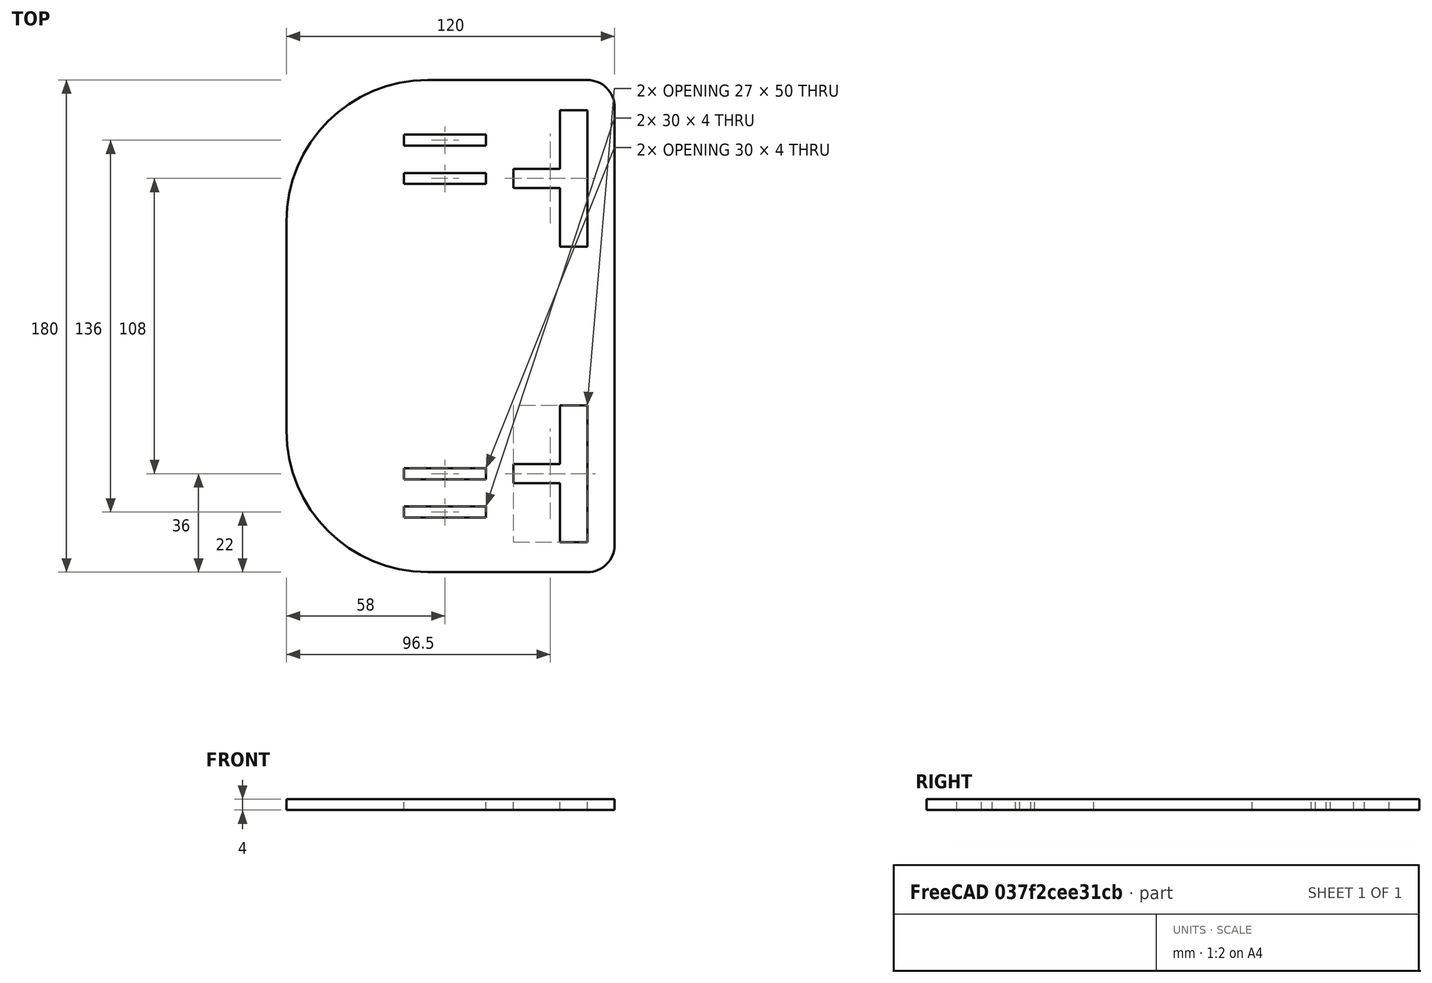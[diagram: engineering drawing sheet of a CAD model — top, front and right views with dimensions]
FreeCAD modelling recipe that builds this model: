
FCSTD DOCUMENT  (FreeCAD 0.21R33771 (Git))
Label: FRAME_BASE
License: All rights reserved
LicenseURL: https://en.wikipedia.org/wiki/All_rights_reserved
objects: Sketcher::SketchObject×2, PartDesign::Pad×1, PartDesign::Body×1
note: 5 computed .brp shape members not serialized (recipe doc carries the construction recipe); baked Part::Feature solids carry a one-line shape summary decoded from their .brp

FEATURE [Sketcher::SketchObject] Sketch  label="A4"
  FullyConstrained = true
  MapMode = 5
  sketch-geometry (4):
    g0: LineSegment StartX=0 StartY=0 StartZ=0 EndX=270 EndY=0 EndZ=0
    g1: LineSegment StartX=270 StartY=0 StartZ=0 EndX=270 EndY=180 EndZ=0
    g2: LineSegment StartX=270 StartY=180 StartZ=0 EndX=0 EndY=180 EndZ=0
    g3: LineSegment StartX=0 StartY=180 StartZ=0 EndX=0 EndY=0 EndZ=0
  constraints (12):
    c: Coincident(g0,g1)
    c: Coincident(g1,g2)
    c: Coincident(g2,g3)
    c: Coincident(g3,g0)
    c: Horizontal(g0)
    c: Horizontal(g2)
    c: Vertical(g1)
    c: Vertical(g3)
    c: PointOnObject(g0,g-2)
    c: DistanceX(g2,g2) = 270
    c: DistanceY(g3,g3) = 180
    c: PointOnObject(g0,g-1)
FEATURE [Sketcher::SketchObject] Sketch001  label="BASE"
  ExternalGeometry = -> [Sketch]
  FullyConstrained = false
  MapMode = 5
  sketch-geometry (57):
    g0: LineSegment StartX=100 StartY=61 StartZ=0 EndX=100 EndY=39.5 EndZ=0
    g1: LineSegment StartX=100 StartY=39.5 StartZ=0 EndX=83 EndY=39.5 EndZ=0
    g2: LineSegment StartX=83 StartY=39.5 StartZ=0 EndX=83 EndY=32.5 EndZ=0
    g3: LineSegment StartX=83 StartY=32.5 StartZ=0 EndX=100 EndY=32.5 EndZ=0
    g4: LineSegment StartX=100 StartY=32.5 StartZ=0 EndX=100 EndY=11 EndZ=0
    g5: LineSegment StartX=100 StartY=11 StartZ=0 EndX=110 EndY=11 EndZ=0
    g6: LineSegment StartX=110 StartY=11 StartZ=0 EndX=110 EndY=61 EndZ=0
    g7: LineSegment StartX=110 StartY=61 StartZ=0 EndX=100 EndY=61 EndZ=0
    g8: LineSegment StartX=100 StartY=119 StartZ=0 EndX=110 EndY=119 EndZ=0
    g9: LineSegment StartX=110 StartY=119 StartZ=0 EndX=110 EndY=169 EndZ=0
    g10: LineSegment StartX=110 StartY=169 StartZ=0 EndX=100 EndY=169 EndZ=0
    g11: LineSegment StartX=100 StartY=169 StartZ=0 EndX=100 EndY=147.5 EndZ=0
    g12: LineSegment StartX=100 StartY=147.5 StartZ=0 EndX=83 EndY=147.5 EndZ=0
    g13: LineSegment StartX=83 StartY=147.5 StartZ=0 EndX=83 EndY=140.5 EndZ=0
    g14: LineSegment StartX=83 StartY=140.5 StartZ=0 EndX=100 EndY=140.5 EndZ=0
    g15: LineSegment StartX=100 StartY=140.5 StartZ=0 EndX=100 EndY=119 EndZ=0
    g16: LineSegment StartX=0 StartY=90 StartZ=0 EndX=0 EndY=128.27 EndZ=0
    g17: LineSegment StartX=51.7304 StartY=180 StartZ=0 EndX=110 EndY=180 EndZ=0
    g18: LineSegment StartX=120 StartY=170 StartZ=0 EndX=120 EndY=10 EndZ=0
    g19: LineSegment StartX=110 StartY=0 StartZ=0 EndX=51.7304 EndY=0 EndZ=0
    g20: LineSegment StartX=0 StartY=51.7304 StartZ=0 EndX=0 EndY=90 EndZ=0
    g21: ArcOfCircle CenterX=51.7304 CenterY=128.27 CenterZ=0 NormalX=0 NormalY=0 NormalZ=1 AngleXU=0 Radius=51.7304 StartAngle=1.5708 EndAngle=3.14159
    g22: GeomPoint X=0 Y=180 Z=0
    g23: ArcOfCircle CenterX=51.7304 CenterY=51.7304 CenterZ=0 NormalX=0 NormalY=0 NormalZ=1 AngleXU=0 Radius=51.7304 StartAngle=3.14159 EndAngle=4.71239
    g24: GeomPoint X=0 Y=0 Z=0
    g25: ArcOfCircle CenterX=110 CenterY=170 CenterZ=0 NormalX=0 NormalY=0 NormalZ=1 AngleXU=0 Radius=10 StartAngle=-9e-16 EndAngle=1.5708
    g26: GeomPoint X=120 Y=180 Z=0
    g27: ArcOfCircle CenterX=110 CenterY=10 CenterZ=0 NormalX=0 NormalY=0 NormalZ=1 AngleXU=0 Radius=10 StartAngle=4.71239 EndAngle=6.28319
    g28: GeomPoint X=120 Y=0 Z=0
    g29: LineSegment StartX=73 StartY=38 StartZ=0 EndX=43 EndY=38 EndZ=0
    g30: LineSegment StartX=43 StartY=38 StartZ=0 EndX=43 EndY=34 EndZ=0
    g31: LineSegment StartX=43 StartY=34 StartZ=0 EndX=73 EndY=34 EndZ=0
    g32: LineSegment StartX=73 StartY=34 StartZ=0 EndX=73 EndY=36 EndZ=0
    g33: LineSegment StartX=73 StartY=36 StartZ=0 EndX=73 EndY=38 EndZ=0
    g34: LineSegment StartX=83 StartY=32.5 StartZ=0 EndX=73 EndY=36 EndZ=0
    g35: LineSegment StartX=73 StartY=36 StartZ=0 EndX=83 EndY=39.5 EndZ=0
    g36: LineSegment StartX=83 StartY=147.5 StartZ=0 EndX=73 EndY=144 EndZ=0
    g37: LineSegment StartX=83 StartY=140.5 StartZ=0 EndX=73 EndY=144 EndZ=0
    g38: LineSegment StartX=73 StartY=144 StartZ=0 EndX=73 EndY=146 EndZ=0
    g39: LineSegment StartX=73 StartY=142 StartZ=0 EndX=73 EndY=144 EndZ=0
    g40: LineSegment StartX=73 StartY=38 StartZ=0 EndX=73 EndY=144 EndZ=0
    g41: LineSegment StartX=73 StartY=146 StartZ=0 EndX=43 EndY=146 EndZ=0
    g42: LineSegment StartX=43 StartY=146 StartZ=0 EndX=43 EndY=142 EndZ=0
    g43: LineSegment StartX=43 StartY=142 StartZ=0 EndX=73 EndY=142 EndZ=0
    g44: LineSegment StartX=43 StartY=38 StartZ=0 EndX=43 EndY=142 EndZ=0
    g45: LineSegment StartX=43 StartY=160 StartZ=0 EndX=43 EndY=156 EndZ=0
    g46: LineSegment StartX=43 StartY=156 StartZ=0 EndX=73 EndY=156 EndZ=0
    g47: LineSegment StartX=73 StartY=156 StartZ=0 EndX=73 EndY=160 EndZ=0
    g48: LineSegment StartX=73 StartY=160 StartZ=0 EndX=43 EndY=160 EndZ=0
    g49: LineSegment StartX=43 StartY=24 StartZ=0 EndX=43 EndY=20 EndZ=0
    g50: LineSegment StartX=43 StartY=20 StartZ=0 EndX=73 EndY=20 EndZ=0
    g51: LineSegment StartX=73 StartY=20 StartZ=0 EndX=73 EndY=24 EndZ=0
    g52: LineSegment StartX=73 StartY=24 StartZ=0 EndX=43 EndY=24 EndZ=0
    g53: LineSegment StartX=43 StartY=24 StartZ=0 EndX=43 EndY=34 EndZ=0
    g54: LineSegment StartX=100 StartY=61 StartZ=0 EndX=100 EndY=90 EndZ=0
    g55: LineSegment StartX=100 StartY=90 StartZ=0 EndX=100 EndY=119 EndZ=0
    g56: LineSegment StartX=0 StartY=90 StartZ=0 EndX=100 EndY=90 EndZ=0
  constraints (154):
    c: Vertical(g0)
    c: Coincident(g1,g0)
    c: Coincident(g2,g1)
    c: Vertical(g2)
    c: Coincident(g3,g2)
    c: Horizontal(g3)
    c: Coincident(g4,g3)
    c: Vertical(g4)
    c: Coincident(g5,g4)
    c: Coincident(g6,g5)
    c: Vertical(g6)
    c: Coincident(g7,g6)
    c: Coincident(g7,g0)
    c: Horizontal(g7)
    c: Horizontal(g1)
    c: Horizontal(g5)
    c: Equal(g0,g4)
    c: Equal(g1,g3)
    c: DistanceY(g2,g2) = 7
    c: DistanceX(g1,g1) = 17
    c: DistanceX(g7,g7) = 10
    c: DistanceY(g6,g6) = 50
    c: Horizontal(g8)
    c: Coincident(g9,g8)
    c: Vertical(g9)
    c: PointOnObject(g10,g9)
    c: Horizontal(g10)
    c: Coincident(g11,g10)
    c: Vertical(g11)
    c: Coincident(g12,g11)
    c: Horizontal(g12)
    c: Coincident(g13,g12)
    c: Vertical(g13)
    c: Coincident(g14,g13)
    c: Horizontal(g14)
    c: Coincident(g15,g14)
    c: Vertical(g15)
    c: Equal(g15,g11)
    c: Equal(g14,g1)
    c: Equal(g8,g7)
    c: Equal(g13,g2)
    c: Vertical(g11,g14)
    c: PointOnObject(g9,g10)
    c: Equal(g6,g9)
    c: DistanceY(g0,g8) = 58
    c: Vertical(g16)
    c: Horizontal(g17)
    c: Vertical(g18)
    c: Horizontal(g19)
    c: Vertical(g20)
    c: DistanceX(g9,g26) = 10
    c: DistanceX(g24,g28) = 120
    c: DistanceY(g24,g22) = 180
    c: PointOnObject(g22,g16)
    c: PointOnObject(g22,g17)
    c: Tangent(g16,g21) = 1.5708
    c: Tangent(g17,g21) = 1.5708
    c: PointOnObject(g24,g20)
    c: PointOnObject(g24,g19)
    c: Tangent(g20,g23) = 1.5708
    c: Tangent(g19,g23) = 1.5708
    c: PointOnObject(g26,g17)
    c: PointOnObject(g26,g18)
    c: Tangent(g17,g25) = 1.5708
    c: Tangent(g18,g25) = 1.5708
    c: PointOnObject(g28,g19)
    c: PointOnObject(g28,g18)
    c: Tangent(g19,g27) = 1.5708
    c: Tangent(g18,g27) = 1.5708
    c: Equal(g20,g16)
    c: Equal(g25,g27)
    c: Radius(g27) = 10
    c: Horizontal(g29)
    c: Coincident(g30,g29)
    c: Vertical(g30)
    c: Coincident(g31,g30)
    c: Horizontal(g31)
    c: Coincident(g32,g31)
    c: Coincident(g33,g32)
    c: Coincident(g33,g29)
    c: Vertical(g32)
    c: Vertical(g33)
    c: Equal(g32,g33)
    c: Coincident(g34,g2)
    c: Coincident(g34,g32)
    c: Equal(g34,g35)
    c: Coincident(g35,g1)
    c: Coincident(g35,g32)
    c: DistanceY(g30,g30) = 4
    c: DistanceX(g31,g31) = 30
    c: DistanceX(g31,g2) = 10
    c: Coincident(g36,g12)
    c: Coincident(g37,g13)
    c: Coincident(g37,g36)
    c: Coincident(g38,g36)
    c: Vertical(g38)
    c: Coincident(g39,g36)
    c: Vertical(g39)
    c: Equal(g39,g38)
    c: Equal(g37,g36)
    c: Coincident(g40,g29)
    c: Vertical(g40)
    c: Vertical(g23,g21)
    c: Coincident(g40,g36)
    c: Coincident(g41,g38)
    c: Horizontal(g41)
    c: Coincident(g42,g41)
    c: Vertical(g42)
    c: Coincident(g43,g42)
    c: Coincident(g43,g39)
    c: Horizontal(g43)
    c: DistanceY(g42,g42) = 4
    c: Coincident(g44,g29)
    c: Coincident(g44,g42)
    c: Vertical(g44)
    c: Coincident(g45,g46)
    c: Coincident(g46,g47)
    c: Coincident(g47,g48)
    c: Coincident(g48,g45)
    c: Vertical(g45)
    c: Vertical(g47)
    c: Horizontal(g46)
    c: Horizontal(g48)
    c: Equal(g41,g46)
    c: Equal(g45,g42)
    c: Vertical(g45,g41)
    c: DistanceY(g41,g45) = 10
    c: Coincident(g49,g50)
    c: Coincident(g50,g51)
    c: Coincident(g51,g52)
    c: Coincident(g52,g49)
    c: Vertical(g49)
    c: Vertical(g51)
    c: Horizontal(g50)
    c: Horizontal(g52)
    c: Equal(g52,g31)
    c: Equal(g49,g30)
    c: Coincident(g53,g49)
    c: Coincident(g53,g30)
    c: Vertical(g53)
    c: DistanceY(g53,g53) = 10
    c: Coincident(g20,g16)
    c: PointOnObject(g19,g-1)
    c: PointOnObject(g16,g-2)
    c: Coincident(g54,g0)
    c: Vertical(g54)
    c: Coincident(g55,g54)
    c: Coincident(g55,g8)
    c: Vertical(g55)
    c: Equal(g55,g54)
    c: Coincident(g56,g16)
    c: Coincident(g56,g54)
    c: Horizontal(g56)
    c: Coincident(g15,g8)
FEATURE [PartDesign::Pad] Pad
  Direction = (0,0,1)
  Length = 4
  Length2 = 10
  Profile = -> Sketch001
  ReferenceAxis = -> Sketch001 [N_Axis]
  Type = 0
FEATURE [PartDesign::Body] Body
  Group = -> [Sketch,Sketch001,Pad]
  Origin = -> Origin
  Tip = -> Pad
